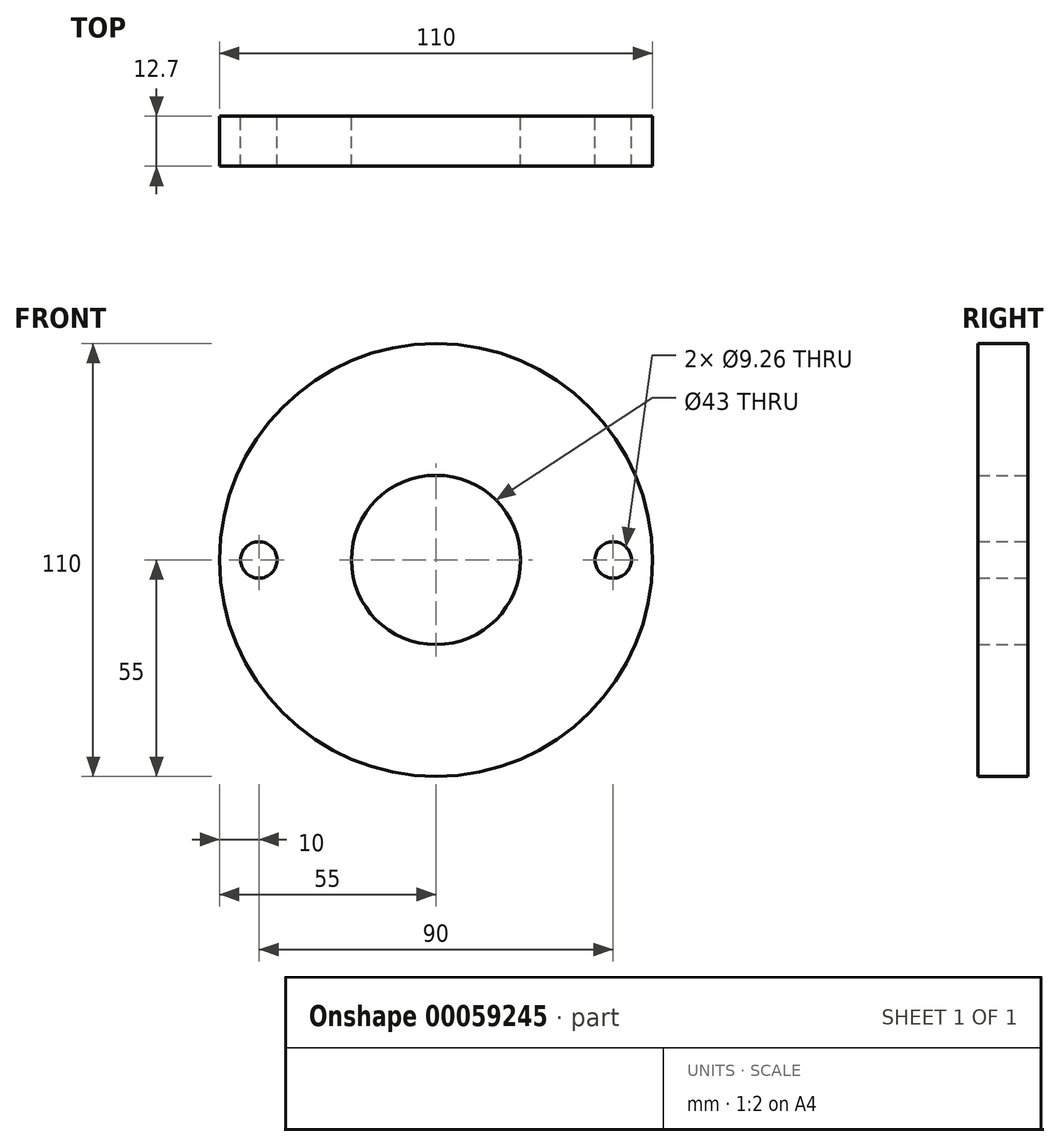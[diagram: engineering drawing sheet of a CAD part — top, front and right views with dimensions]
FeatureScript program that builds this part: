
annotation { "Feature Type Name" : "Feature", "Feature Type Description" : "" }
export const myFeature = defineFeature(function(context is Context, id is Id, definition is map)
    precondition{}
    {
        {
            var Q0;
            Q0=qCreatedBy(makeId("Front.planeOp"),FACE);
            var sketch = newSketch(context, id + "F0", { "sketchPlane" : qUnion([Q0])});
            skCircle(sketch, "E0", {"center": v(0, 0) * mm, "radius": 55 * mm});
            skCircle(sketch, "E1", {"center": v(0, 0) * mm, "radius": 21.5 * mm});
            skCircle(sketch, "E2", {"center": v(45, 0) * mm, "radius": 4.63 * mm});
            skCircle(sketch, "E3", {"center": v(-45, 0) * mm, "radius": 4.63 * mm});
            skLineSegment(sketch, "E4", {"start": v(55, 0) * mm, "end": v(45, 0) * mm});
            skLineSegment(sketch, "E5", {"start": v(-55, 0) * mm, "end": v(-45, 0) * mm});
            skSolve(sketch);
        }
        {
            var Q0;
            Q0=makeQuery(id+"F0.imprint","IMPRINT",FACE,{"disambiguationData":[TD([[makeQuery(id+"F0.imprint","IMPRINT",EDGE,{"derivedFrom":sQuery(id+"F0.wireOp",EDGE,"E1")}),-1.0]])]});
            extrude(context, id + "F1", {"entities" : qUnion([Q0]), "depth" : 12.7 * mm});
        }
    });
